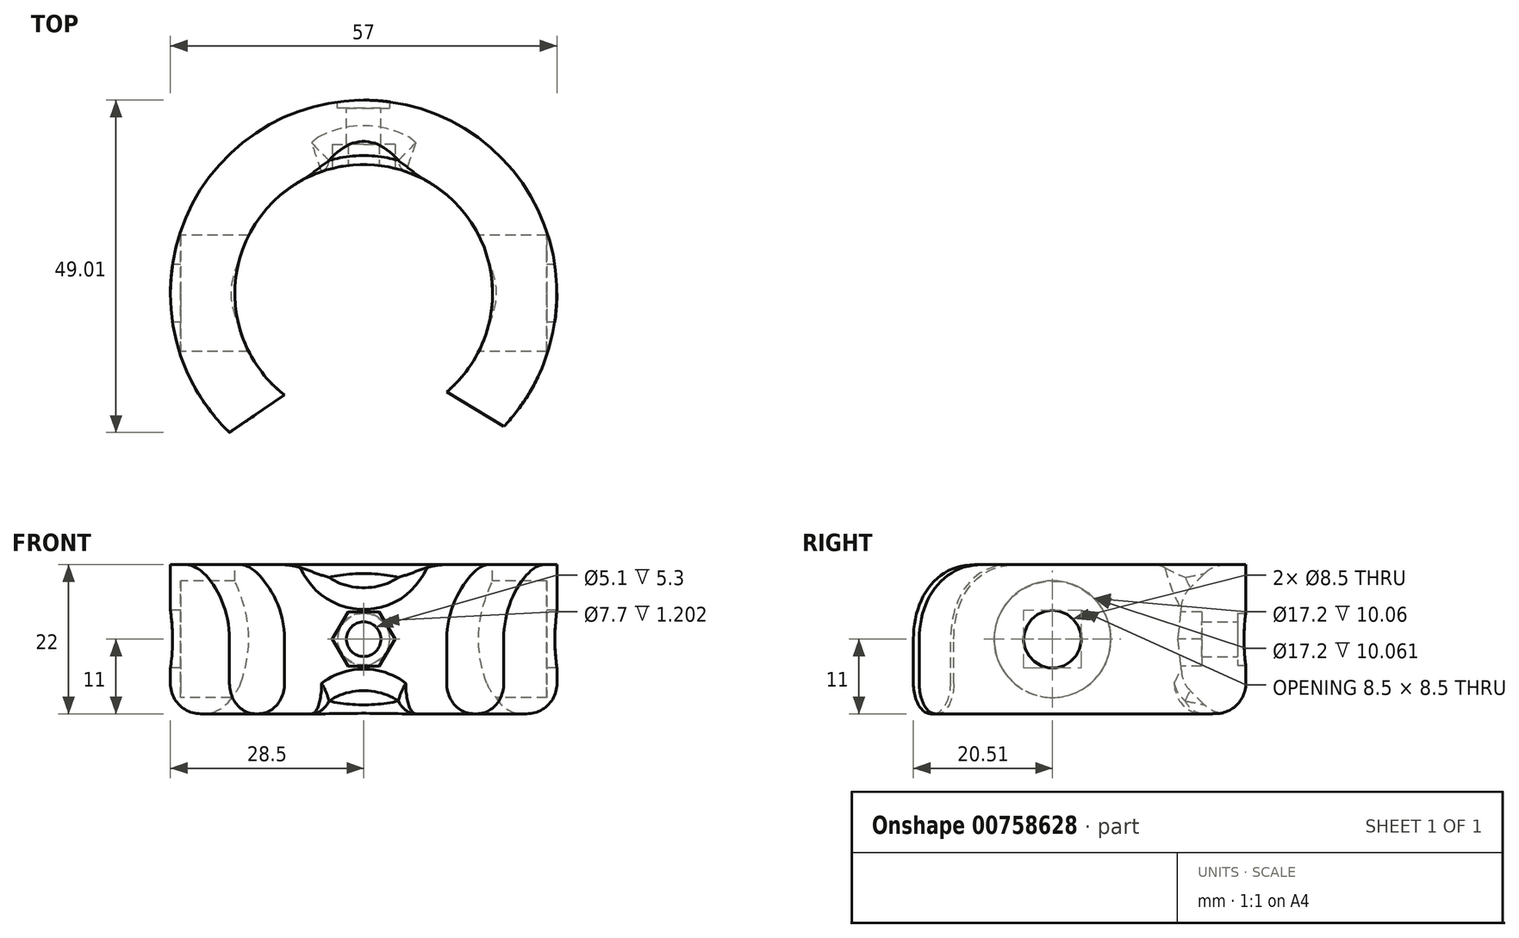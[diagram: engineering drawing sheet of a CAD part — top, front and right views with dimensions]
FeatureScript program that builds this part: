
annotation { "Feature Type Name" : "Feature", "Feature Type Description" : "" }
export const myFeature = defineFeature(function(context is Context, id is Id, definition is map)
    precondition{}
    {
        {
            var Q0;
            Q0=qCreatedBy(makeId("Top.planeOp"),FACE);
            var sketch = newSketch(context, id + "F0", { "sketchPlane" : qUnion([Q0])});
            skCircle(sketch, "E0", {"center": v(0, 0) * mm, "radius": 28.5 * mm});
            skSolve(sketch);
        }
        {
            var Q0;
            Q0=makeQuery(id+"F0.imprint","IMPRINT",FACE,{"disambiguationData":[TD([[makeQuery(id+"F0.imprint","IMPRINT",EDGE,{"derivedFrom":sQuery(id+"F0.wireOp",EDGE,"E0")}),1.0]])]});
            extrude(context, id + "F1", {"entities" : qUnion([Q0]), "depth" : 22 * mm, "offsetDistance" : 25 * mm});
        }
        {
            var Q0;
            Q0=makeQuery(id+"F1.opExtrude","CAP_FACE",FACE,{"disambiguationData":[OSD([sQuery(id+"F0.wireOp",EDGE,"E0")])],"isStart":false});
            var sketch = newSketch(context, id + "F2", { "sketchPlane" : qUnion([Q0])});
            skCircle(sketch, "E1", {"center": v(0, 0) * mm, "radius": 19 * mm});
            skSolve(sketch);
        }
        {
            var Q0;
            Q0=makeQuery(id+"F2.imprint","IMPRINT",FACE,{"disambiguationData":[TD([[makeQuery(id+"F2.imprint","IMPRINT",EDGE,{"derivedFrom":sQuery(id+"F2.wireOp",EDGE,"E1")}),1.0]])]});
            extrude(context, id + "F3", {"entities" : qUnion([Q0]), "operationType" : NewBodyOperationType.REMOVE, "endBound" : BoundingType.THROUGH_ALL, "oppositeDirection" : true, "depth" : 25 * mm, "offsetDistance" : 25 * mm});
        }
        {
            var Q0;
            Q0=qCreatedBy(makeId("Right.planeOp"),FACE);
            var sketch = newSketch(context, id + "F4", { "sketchPlane" : qUnion([Q0])});
            skCircle(sketch, "E2", {"center": v(0, 11) * mm, "radius": 8.6 * mm});
            skSolve(sketch);
        }
        {
            var Q0;
            Q0=makeQuery(id+"F4.imprint","IMPRINT",FACE,{"disambiguationData":[TD([[makeQuery(id+"F4.imprint","IMPRINT",EDGE,{"derivedFrom":sQuery(id+"F4.wireOp",EDGE,"E2")}),1.0]])]});
            extrude(context, id + "F5", {"entities" : qUnion([Q0]), "operationType" : NewBodyOperationType.REMOVE, "depth" : 54 * mm, "offsetDistance" : 25 * mm, "symmetric" : true});
        }
        {
            var Q0;
            Q0=qCreatedBy(makeId("Top.planeOp"),FACE);
            var sketch = newSketch(context, id + "F6", { "sketchPlane" : qUnion([Q0])});
            skLineSegment(sketch, "E3", {"start": v(0, -7.12) * mm, "end": v(-67.6, -52.85) * mm});
            skLineSegment(sketch, "E4", {"start": v(-67.6, -52.85) * mm, "end": v(75.43, -52.85) * mm});
            skLineSegment(sketch, "E5", {"start": v(75.43, -52.85) * mm, "end": v(0, -7.12) * mm});
            skSolve(sketch);
        }
        {
            var Q0;
            Q0 = qSketchRegion(id + "F6", true);
            extrude(context, id + "F7", {"entities" : qUnion([Q0]), "operationType" : NewBodyOperationType.REMOVE, "depth" : 30 * mm, "offsetDistance" : 25 * mm});
        }
        {
            var Q0;
            Q0=qCreatedBy(makeId("Front.planeOp"),FACE);
            var sketch = newSketch(context, id + "F8", { "sketchPlane" : qUnion([Q0])});
            skLineSegment(sketch, "E6", {"start": v(-34.26, 11) * mm, "end": v(40.8, 11) * mm});
            skSolve(sketch);
        }
        {
            var Q0;
            Q0=qCreatedBy(makeId("Front.planeOp"),FACE);
            var Q1;
            Q1=sQuery(id+"F8.wireOp",EDGE,"E6");
            cPlane(context, id + "F9", {"entities" : qUnion([Q0, Q1]), "cplaneType" : CPlaneType.LINE_ANGLE, "offset" : 25 * mm, "angle" : 45 * degree, "width" : 150 * mm, "height" : 150 * mm});
        }
        {
            var Q0;
            Q0=qCreatedBy(id+"F9.planeOp",FACE);
            var sketch = newSketch(context, id + "F10", { "sketchPlane" : qUnion([Q0])});
            skCircle(sketch, "E7", {"center": v(0, 7.78) * mm, "radius": 9 * mm});
            skSolve(sketch);
        }
        {
            var Q0;
            Q0=makeQuery(id+"F10.imprint","IMPRINT",FACE,{"disambiguationData":[TD([[makeQuery(id+"F10.imprint","IMPRINT",EDGE,{"derivedFrom":sQuery(id+"F10.wireOp",EDGE,"E7")}),1.0]])]});
            extrude(context, id + "F11", {"entities" : qUnion([Q0]), "operationType" : NewBodyOperationType.REMOVE, "endBound" : BoundingType.THROUGH_ALL, "depth" : 30 * mm, "offsetDistance" : 25 * mm});
        }
        {
            var Q0;
            Q0=qCreatedBy(makeId("Front.planeOp"),FACE);
            var Q1;
            Q1=sQuery(id+"F8.wireOp",EDGE,"E6");
            cPlane(context, id + "F12", {"entities" : qUnion([Q0, Q1]), "cplaneType" : CPlaneType.LINE_ANGLE, "offset" : 25 * mm, "angle" : 45 * degree, "oppositeDirection" : true, "width" : 150 * mm, "height" : 150 * mm});
        }
        {
            var Q0;
            Q0=qCreatedBy(id+"F12.planeOp",FACE);
            var sketch = newSketch(context, id + "F13", { "sketchPlane" : qUnion([Q0])});
            skCircle(sketch, "E8", {"center": v(0, 7.78) * mm, "radius": 9 * mm});
            skSolve(sketch);
        }
        {
            var Q0;
            Q0=qCreatedBy(makeId("Front.planeOp"),FACE);
            cPlane(context, id + "F14", {"entities" : qUnion([Q0]), "cplaneType" : CPlaneType.OFFSET, "offset" : 28.5 * mm, "oppositeDirection" : true, "width" : 150 * mm, "height" : 150 * mm});
        }
        {
            var Q0;
            Q0=qCreatedBy(id+"F14.planeOp",FACE);
            var sketch = newSketch(context, id + "F15", { "sketchPlane" : qUnion([Q0])});
            skCircle(sketch, "E9", {"center": v(0, 11) * mm, "radius": 3.85 * mm});
            skSolve(sketch);
        }
        {
            var Q0;
            Q0=makeQuery(id+"F15.imprint","IMPRINT",FACE,{"disambiguationData":[TD([[makeQuery(id+"F15.imprint","IMPRINT",EDGE,{"derivedFrom":sQuery(id+"F15.wireOp",EDGE,"E9")}),1.0]])]});
            extrude(context, id + "F16", {"entities" : qUnion([Q0]), "operationType" : NewBodyOperationType.REMOVE, "depth" : 1.2 * mm, "offsetDistance" : 25 * mm});
        }
        {
            var Q0;
            Q0=makeQuery(id+"F16.boolean.opBoolean","COPY",FACE,{"derivedFrom":makeQuery(id+"F16.opExtrude","CAP_FACE",FACE,{"disambiguationData":[OSD([sQuery(id+"F15.wireOp",EDGE,"E9")])],"isStart":false})});
            var sketch = newSketch(context, id + "F17", { "sketchPlane" : qUnion([Q0])});
            skCircle(sketch, "E10", {"center": v(0, 11) * mm, "radius": 2.55 * mm});
            skSolve(sketch);
        }
        {
            var Q0;
            Q0=makeQuery(id+"F17.imprint","IMPRINT",FACE,{"disambiguationData":[TD([[makeQuery(id+"F17.imprint","IMPRINT",EDGE,{"derivedFrom":sQuery(id+"F17.wireOp",EDGE,"E10")}),1.0]])]});
            extrude(context, id + "F18", {"entities" : qUnion([Q0]), "operationType" : NewBodyOperationType.REMOVE, "endBound" : BoundingType.THROUGH_ALL, "oppositeDirection" : true, "depth" : 25 * mm, "offsetDistance" : 25 * mm});
        }
        {
            var Q0;
            Q0=qCreatedBy(makeId("Front.planeOp"),FACE);
            cPlane(context, id + "F19", {"entities" : qUnion([Q0]), "cplaneType" : CPlaneType.OFFSET, "offset" : 18.5 * mm, "oppositeDirection" : true, "width" : 150 * mm, "height" : 150 * mm});
        }
        {
            var Q0;
            Q0=qCreatedBy(id+"F19.planeOp",FACE);
            var sketch = newSketch(context, id + "F20", { "sketchPlane" : qUnion([Q0])});
            skCircle(sketch, "E11.cCircle", {"center": v(0, 11) * mm, "radius": 4 * mm, "construction": true});
            skLineSegment(sketch, "E11.0", {"start": v(2.3, 7) * mm, "end": v(-2.3, 7) * mm});
            skLineSegment(sketch, "E11.1", {"start": v(-2.3, 7) * mm, "end": v(-4.62, 11) * mm});
            skLineSegment(sketch, "E11.2", {"start": v(-4.62, 11) * mm, "end": v(-2.3, 15) * mm});
            skLineSegment(sketch, "E11.3", {"start": v(-2.3, 15) * mm, "end": v(2.3, 15) * mm});
            skLineSegment(sketch, "E11.4", {"start": v(2.3, 15) * mm, "end": v(4.62, 11) * mm});
            skLineSegment(sketch, "E11.5", {"start": v(4.62, 11) * mm, "end": v(2.3, 7) * mm});
            skPoint(sketch, "E11.0.midPoint", {"position": v(0, 7) * mm});
            skSolve(sketch);
        }
        {
            var Q0;
            Q0 = qSketchRegion(id + "F20", true);
            var Q1;
            Q1 = qConstructionFilter(qBodyType(qCreatedBy(id + "F20" ,EDGE), BodyType.WIRE), ConstructionObject.NO);
            extrude(context, id + "F21", {"entities" : qUnion([Q0]), "operationType" : NewBodyOperationType.REMOVE, "surfaceEntities" : qUnion([Q1]), "oppositeDirection" : true, "depth" : 7 * mm, "offsetDistance" : 25 * mm, "symmetric" : true});
        }
        {
            var Q0;
            Q0=makeQuery(id+"F13.imprint","IMPRINT",FACE,{"disambiguationData":[TD([[makeQuery(id+"F13.imprint","IMPRINT",EDGE,{"derivedFrom":sQuery(id+"F13.wireOp",EDGE,"E8")}),1.0]])]});
            extrude(context, id + "F22", {"entities" : qUnion([Q0]), "operationType" : NewBodyOperationType.REMOVE, "endBound" : BoundingType.THROUGH_ALL, "depth" : 25 * mm, "offsetDistance" : 25 * mm});
        }
        {
            var Q0;
            Q0=qCreatedBy(makeId("Right.planeOp"),FACE);
            var sketch = newSketch(context, id + "F23", { "sketchPlane" : qUnion([Q0])});
            skCircle(sketch, "E12", {"center": v(0, 11) * mm, "radius": 4.25 * mm});
            skSolve(sketch);
        }
        {
            var Q0;
            Q0=makeQuery(id+"F23.imprint","IMPRINT",FACE,{"disambiguationData":[TD([[makeQuery(id+"F23.imprint","IMPRINT",EDGE,{"derivedFrom":sQuery(id+"F23.wireOp",EDGE,"E12")}),1.0]])]});
            extrude(context, id + "F24", {"entities" : qUnion([Q0]), "operationType" : NewBodyOperationType.REMOVE, "depth" : 60 * mm, "offsetDistance" : 25 * mm, "symmetric" : true});
        }
        {
            var Q0;
            Q0=makeQuery(id+"F7.boolean.opBoolean","COPY",EDGE,{"derivedFrom":makeQuery(id+"F7.opExtrude","CAP_EDGE",EDGE,{"disambiguationData":[OSD([sQuery(id+"F6.wireOp",EDGE,"E5")])],"isStart":true})});
            var Q1;
            Q1=makeQuery(id+"F7.boolean.opBoolean","INTERSECT",EDGE,{"derivedFrom":[makeQuery(id+"F1.opExtrude","CAP_FACE",FACE,{"disambiguationData":[OSD([sQuery(id+"F0.wireOp",EDGE,"E0")])],"isStart":false}),makeQuery(id+"F7.opExtrude","SWEPT_FACE",FACE,{"disambiguationData":[OSD([sQuery(id+"F6.wireOp",EDGE,"E5")])]})]});
            var Q2;
            Q2=makeQuery(id+"F7.boolean.opBoolean","COPY",EDGE,{"derivedFrom":makeQuery(id+"F7.opExtrude","CAP_EDGE",EDGE,{"disambiguationData":[OSD([sQuery(id+"F6.wireOp",EDGE,"E3")])],"isStart":true})});
            var Q3;
            Q3=makeQuery(id+"F7.boolean.opBoolean","INTERSECT",EDGE,{"derivedFrom":[makeQuery(id+"F1.opExtrude","CAP_FACE",FACE,{"disambiguationData":[OSD([sQuery(id+"F0.wireOp",EDGE,"E0")])],"isStart":false}),makeQuery(id+"F7.opExtrude","SWEPT_FACE",FACE,{"disambiguationData":[OSD([sQuery(id+"F6.wireOp",EDGE,"E3")])]})]});
            fillet(context, id + "F25", {"entities" : qUnion([Q0, Q1, Q2, Q3]), "radius" : 11 * mm, "tangentPropagation" : true, "allowEdgeOverflow" : false});
        }
        {
            var Q0;
            {var subQ0=makeQuery(id+"F1.opExtrude","CAP_FACE",FACE,{"disambiguationData":[OSD([sQuery(id+"F0.wireOp",EDGE,"E0")])],"isStart":true});var subQ1=makeQuery(id+"F3.opExtrude","SWEPT_FACE",FACE,{"disambiguationData":[OSD([sQuery(id+"F2.wireOp",EDGE,"E1")])]});Q0=makeQuery(id+"F22.boolean.opBoolean","SPLIT",EDGE,{"disambiguationData":[TD([makeQuery(id+"F7.boolean.opBoolean","COPY",FACE,{"derivedFrom":makeQuery(id+"F7.opExtrude","SWEPT_FACE",FACE,{"disambiguationData":[OSD([sQuery(id+"F6.wireOp",EDGE,"E5")])]})})])],"derivedFrom":makeQuery(id+"F3.boolean.opBoolean","INTERSECT",EDGE,{"derivedFrom":[subQ0,subQ1]})});}
            var Q1;
            Q1=makeQuery(id+"F1.opExtrude","CAP_EDGE",EDGE,{"disambiguationData":[OSD([sQuery(id+"F0.wireOp",EDGE,"E0")])],"isStart":true});
            var Q2;
            {var subQ0=makeQuery(id+"F1.opExtrude","CAP_FACE",FACE,{"disambiguationData":[OSD([sQuery(id+"F0.wireOp",EDGE,"E0")])],"isStart":true});var subQ1=makeQuery(id+"F3.opExtrude","SWEPT_FACE",FACE,{"disambiguationData":[OSD([sQuery(id+"F2.wireOp",EDGE,"E1")])]});Q2=makeQuery(id+"F22.boolean.opBoolean","SPLIT",EDGE,{"disambiguationData":[TD([makeQuery(id+"F7.boolean.opBoolean","COPY",FACE,{"derivedFrom":makeQuery(id+"F7.opExtrude","SWEPT_FACE",FACE,{"disambiguationData":[OSD([sQuery(id+"F6.wireOp",EDGE,"E3")])]})})])],"derivedFrom":makeQuery(id+"F3.boolean.opBoolean","INTERSECT",EDGE,{"derivedFrom":[subQ0,subQ1]})});}
            var Q3;
            Q3=makeQuery(id+"F22.boolean.opBoolean","INTERSECT",EDGE,{"derivedFrom":[makeQuery(id+"F3.boolean.opBoolean","COPY",FACE,{"derivedFrom":makeQuery(id+"F3.opExtrude","SWEPT_FACE",FACE,{"disambiguationData":[OSD([sQuery(id+"F2.wireOp",EDGE,"E1")])]})}),makeQuery(id+"F22.opExtrude","SWEPT_FACE",FACE,{"disambiguationData":[OSD([sQuery(id+"F13.wireOp",EDGE,"E8")])]})]});
            var Q4;
            Q4=makeQuery(id+"F22.boolean.opBoolean","INTERSECT",EDGE,{"derivedFrom":[makeQuery(id+"F1.opExtrude","CAP_FACE",FACE,{"disambiguationData":[OSD([sQuery(id+"F0.wireOp",EDGE,"E0")])],"isStart":true}),makeQuery(id+"F22.opExtrude","SWEPT_FACE",FACE,{"disambiguationData":[OSD([sQuery(id+"F13.wireOp",EDGE,"E8")])]})]});
            var Q5;
            Q5=makeQuery(id+"F11.boolean.opBoolean","INTERSECT",EDGE,{"derivedFrom":[makeQuery(id+"F1.opExtrude","CAP_FACE",FACE,{"disambiguationData":[OSD([sQuery(id+"F0.wireOp",EDGE,"E0")])],"isStart":false}),makeQuery(id+"F11.opExtrude","SWEPT_FACE",FACE,{"disambiguationData":[OSD([sQuery(id+"F10.wireOp",EDGE,"E7")])]})]});
            var Q6;
            Q6=makeQuery(id+"F11.boolean.opBoolean","INTERSECT",EDGE,{"derivedFrom":[makeQuery(id+"F3.boolean.opBoolean","COPY",FACE,{"derivedFrom":makeQuery(id+"F3.opExtrude","SWEPT_FACE",FACE,{"disambiguationData":[OSD([sQuery(id+"F2.wireOp",EDGE,"E1")])]})}),makeQuery(id+"F11.opExtrude","SWEPT_FACE",FACE,{"disambiguationData":[OSD([sQuery(id+"F10.wireOp",EDGE,"E7")])]})]});
            fillet(context, id + "F26", {"entities" : qUnion([Q0, Q1, Q2, Q3, Q4, Q5, Q6]), "radius" : 4.5 * mm, "tangentPropagation" : true, "allowEdgeOverflow" : false});
        }
    });
